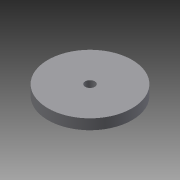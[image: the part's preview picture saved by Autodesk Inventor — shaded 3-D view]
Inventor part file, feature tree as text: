
AUTODESK INVENTOR PART (.ipt)
format: ipt  version: 2013 SP1 (Build 170176100, 176)  size: 77,312 bytes
history: native  units: mm
features: extrude x1, sketch x1
ambient origin geometry x8: Origin, YZ Plane, XZ Plane, XY Plane, X Axis, Y Axis, Z Axis, Center Point
bodies: Solid1 (feature_tree)
feature tree (2):
  extrude  "Extrusion1"  Depth=2.8mm
  sketch  "Sketch1"  dims[d3=24.5mm d4=2.8mm d5=3.0mm d6=0.0mm]
